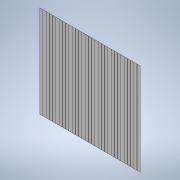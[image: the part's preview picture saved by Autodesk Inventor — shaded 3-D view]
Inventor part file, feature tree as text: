
AUTODESK INVENTOR PART (.ipt)
format: ipt  version: 2021 (Build 250183000, 183)  size: 222,720 bytes
history: native  units: in
note: dims shown in document units (in); Inventor stores cm internally (conversion verified against a paired STEP export)
features: extrude x3, sketch x3, pattern_linear x1, projected_geometry x1
ambient origin geometry x8: Origin, YZ Plane, XZ Plane, XY Plane, X Axis, Y Axis, Z Axis, Center Point
bodies: Solid1 (feature_tree)
feature tree (8):
  extrude  "Extrusion1"  Depth=3.0in
  extrude  "Extrusion2"  Depth=0.1in
  pattern_linear  "Rectangular Pattern1"  Count1=31 Spacing1=0.106in
  extrude  "Extrusion3"  Depth=0.106in TaperAngle=0.0deg
  sketch  "Sketch1"  dims[d0=4.0in d1=3.0in]
  sketch  "Sketch2"  dims[d2=0.04in d3=0.0in d4=0.1in]
  projected_geometry  "Projected Loop1"
  sketch  "Sketch3"  dims[d5=0.0015in d6=0.0in d7=12.2047in d9=0.106in d10=1.0in d11=0.0in]
